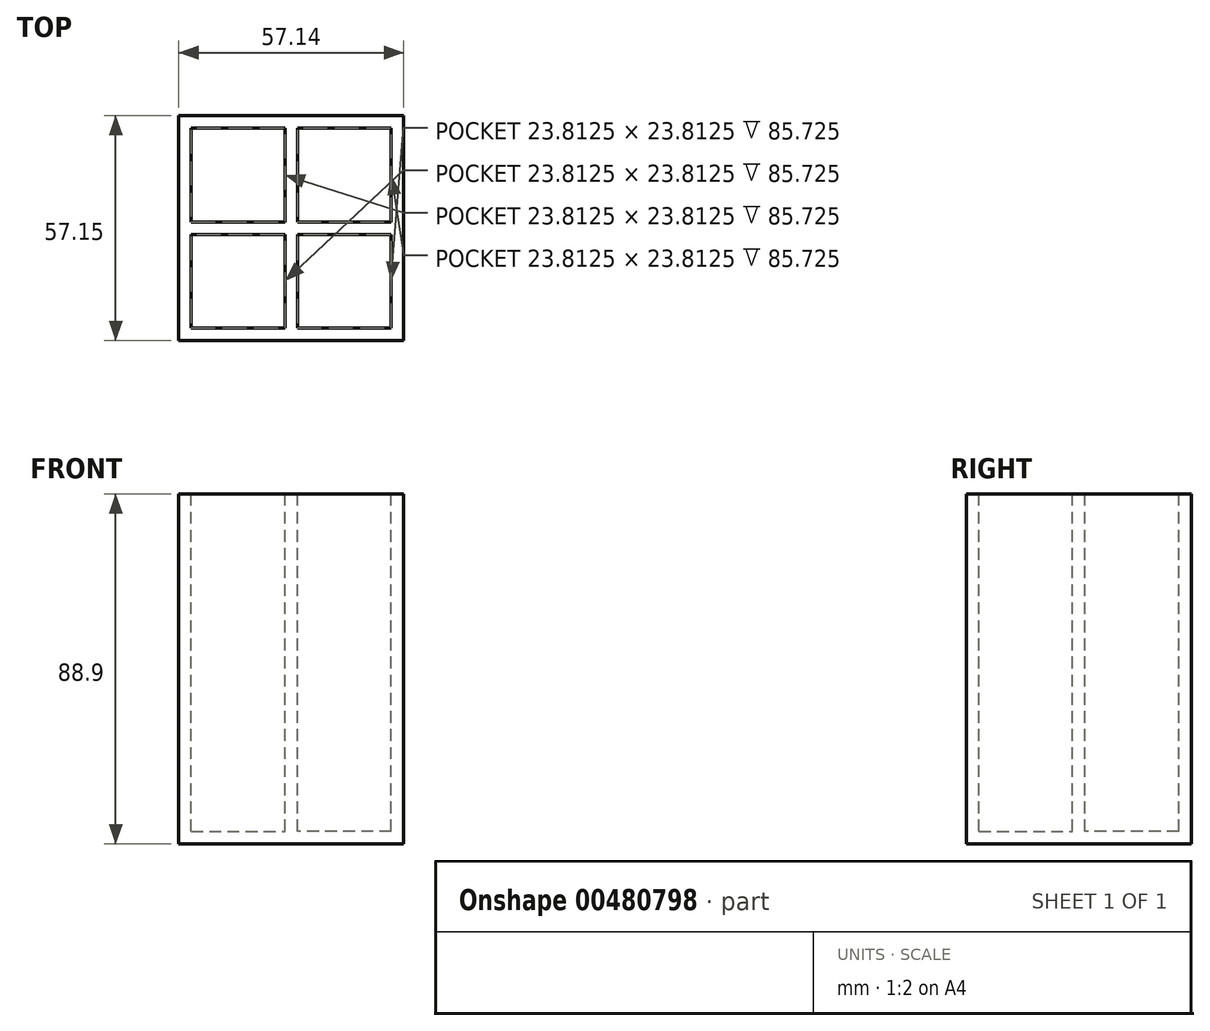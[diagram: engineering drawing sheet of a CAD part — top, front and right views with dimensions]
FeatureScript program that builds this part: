
annotation { "Feature Type Name" : "Feature", "Feature Type Description" : "" }
export const myFeature = defineFeature(function(context is Context, id is Id, definition is map)
    precondition{}
    {
        {
            var Q0;
            Q0=qCreatedBy(makeId("Front.planeOp"),FACE);
            var sketch = newSketch(context, id + "F0", { "sketchPlane" : qUnion([Q0])});
            skLineSegment(sketch, "E0.bottom", {"start": v(-28.57, 44.45) * mm, "end": v(28.58, 44.45) * mm});
            skLineSegment(sketch, "E0.top", {"start": v(-28.58, -44.45) * mm, "end": v(28.57, -44.45) * mm});
            skLineSegment(sketch, "E0.left", {"start": v(-28.57, 44.45) * mm, "end": v(-28.58, -44.45) * mm});
            skLineSegment(sketch, "E0.right", {"start": v(28.58, 44.45) * mm, "end": v(28.57, -44.45) * mm});
            skPoint(sketch, "E0.middle", {"position": v(0, 0) * mm});
            skSolve(sketch);
        }
        {
            var Q0;
            Q0 = qSketchRegion(id + "F0", true);
            extrude(context, id + "F1", {"entities" : qUnion([Q0]), "depth" : 57.15 * mm});
        }
        {
            var Q0;
            Q0=makeQuery(id+"F1.opExtrude","SWEPT_FACE",FACE,{"disambiguationData":[OSD([sQuery(id+"F0.wireOp",EDGE,"E0.bottom")])]});
            var sketch = newSketch(context, id + "F2", { "sketchPlane" : qUnion([Q0])});
            skLineSegment(sketch, "E1.bottom", {"start": v(25.4, -53.98) * mm, "end": v(1.59, -53.98) * mm});
            skLineSegment(sketch, "E1.top", {"start": v(25.4, -30.16) * mm, "end": v(1.59, -30.16) * mm});
            skLineSegment(sketch, "E1.left", {"start": v(25.4, -53.98) * mm, "end": v(25.4, -30.16) * mm});
            skLineSegment(sketch, "E1.right", {"start": v(1.59, -53.98) * mm, "end": v(1.59, -30.16) * mm});
            skLineSegment(sketch, "E2.bottom", {"start": v(-25.4, -53.98) * mm, "end": v(-1.59, -53.98) * mm});
            skLineSegment(sketch, "E2.top", {"start": v(-25.4, -30.16) * mm, "end": v(-1.59, -30.16) * mm});
            skLineSegment(sketch, "E2.left", {"start": v(-25.4, -53.98) * mm, "end": v(-25.4, -30.16) * mm});
            skLineSegment(sketch, "E2.right", {"start": v(-1.59, -53.98) * mm, "end": v(-1.59, -30.16) * mm});
            skLineSegment(sketch, "E3.bottom", {"start": v(-25.4, -3.18) * mm, "end": v(-1.59, -3.17) * mm});
            skLineSegment(sketch, "E3.top", {"start": v(-25.4, -26.99) * mm, "end": v(-1.59, -26.99) * mm});
            skLineSegment(sketch, "E3.left", {"start": v(-25.4, -3.18) * mm, "end": v(-25.4, -26.99) * mm});
            skLineSegment(sketch, "E3.right", {"start": v(-1.59, -3.17) * mm, "end": v(-1.59, -26.99) * mm});
            skLineSegment(sketch, "E4.bottom", {"start": v(25.4, -3.17) * mm, "end": v(1.59, -3.18) * mm});
            skLineSegment(sketch, "E4.top", {"start": v(25.4, -26.99) * mm, "end": v(1.59, -26.99) * mm});
            skLineSegment(sketch, "E4.left", {"start": v(25.4, -3.17) * mm, "end": v(25.4, -26.99) * mm});
            skLineSegment(sketch, "E4.right", {"start": v(1.59, -3.18) * mm, "end": v(1.59, -26.99) * mm});
            skSolve(sketch);
        }
        {
            var Q0;
            Q0 = qSketchRegion(id + "F2", true);
            extrude(context, id + "F3", {"entities" : qUnion([Q0]), "operationType" : NewBodyOperationType.REMOVE, "oppositeDirection" : true, "depth" : 85.72 * mm});
        }
    });
